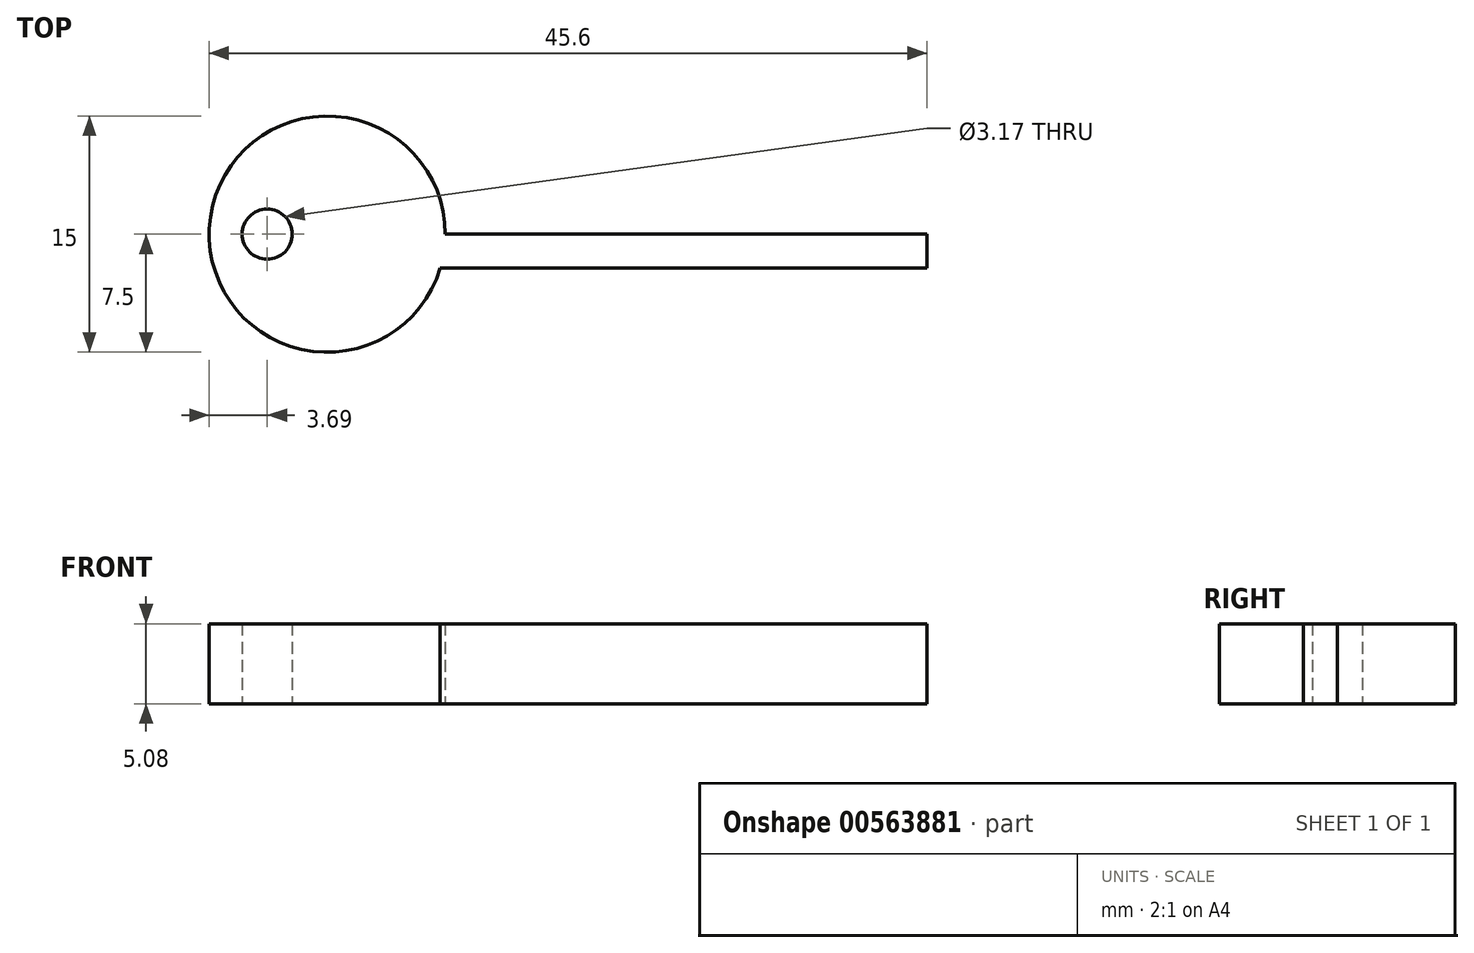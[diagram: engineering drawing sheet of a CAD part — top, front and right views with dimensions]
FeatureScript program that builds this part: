
annotation { "Feature Type Name" : "Feature", "Feature Type Description" : "" }
export const myFeature = defineFeature(function(context is Context, id is Id, definition is map)
    precondition{}
    {
        {
            var Q0;
            Q0=qCreatedBy(makeId("Top.planeOp"),FACE);
            var sketch = newSketch(context, id + "F0", { "sketchPlane" : qUnion([Q0])});
            skCircle(sketch, "E0", {"center": v(0, 0) * mm, "radius": 7.5 * mm});
            skCircle(sketch, "E1", {"center": v(-3.81, 0) * mm, "radius": 1.59 * mm});
            skLineSegment(sketch, "E2.bottom", {"start": v(-15.78, 0) * mm, "end": v(-15.78, 0) * mm});
            skLineSegment(sketch, "E2.top", {"start": v(-15.78, 5.08) * mm, "end": v(-15.78, 5.08) * mm});
            skPoint(sketch, "E2.middle", {"position": v(-15.78, 2.54) * mm});
            skPoint(sketch, "E3.middle", {"position": v(-15.93, 0.97) * mm});
            skLineSegment(sketch, "E4.bottom", {"start": v(0, 0) * mm, "end": v(38.1, 0) * mm});
            skLineSegment(sketch, "E4.top", {"start": v(0, -2.15) * mm, "end": v(38.1, -2.15) * mm});
            skLineSegment(sketch, "E4.left", {"start": v(0, 0) * mm, "end": v(0, -2.15) * mm});
            skLineSegment(sketch, "E4.right", {"start": v(38.1, 0) * mm, "end": v(38.1, -2.15) * mm});
            skSolve(sketch);
        }
        {
            var Q0;
            Q0 = qSketchRegion(id + "F0", true);
            extrude(context, id + "F1", {"entities" : qUnion([Q0]), "depth" : 5.08 * mm, "offsetDistance" : 25.4 * mm});
        }
    });
